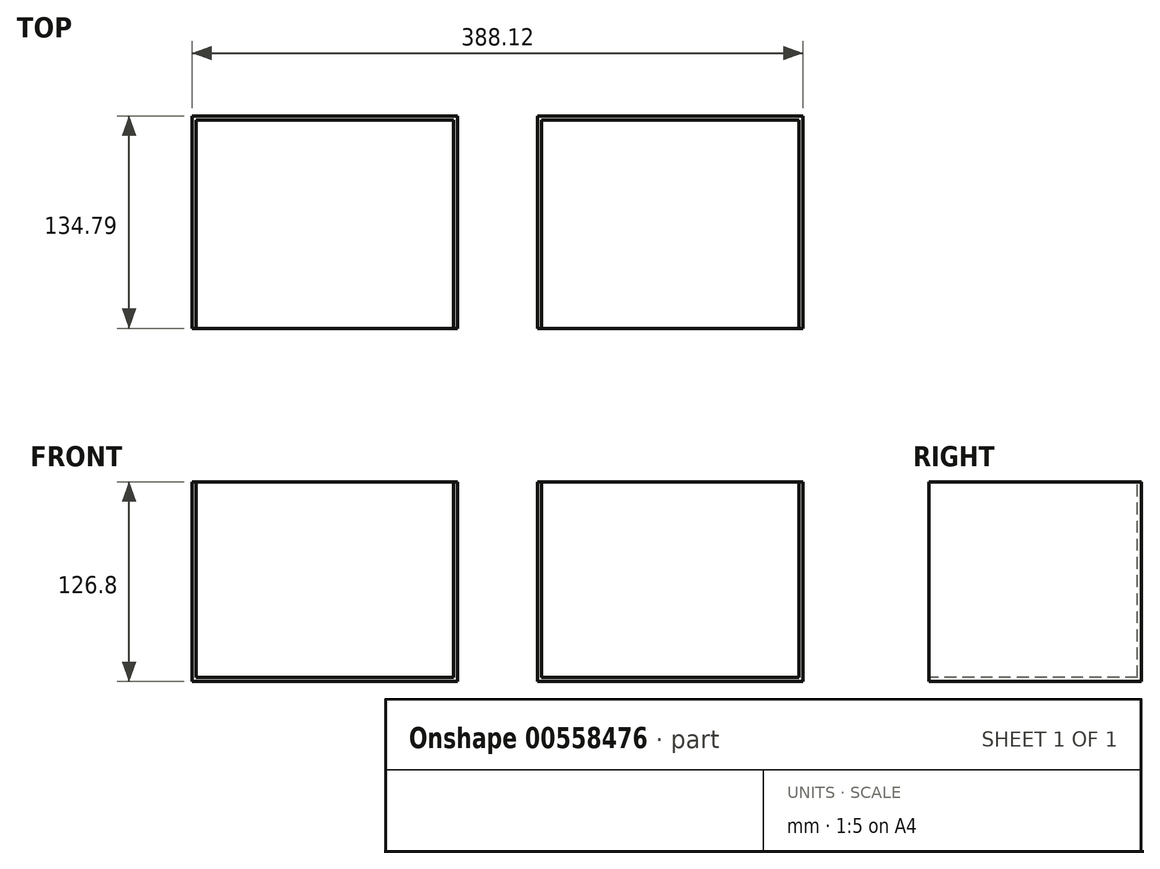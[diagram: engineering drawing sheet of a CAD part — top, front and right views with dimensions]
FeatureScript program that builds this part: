
annotation { "Feature Type Name" : "Feature", "Feature Type Description" : "" }
export const myFeature = defineFeature(function(context is Context, id is Id, definition is map)
    precondition{}
    {
        {
            var Q0;
            Q0=qCreatedBy(makeId("Front.planeOp"),FACE);
            var sketch = newSketch(context, id + "F0", { "sketchPlane" : qUnion([Q0])});
            skLineSegment(sketch, "E0.bottom", {"start": v(60.56, 0) * mm, "end": v(-108.1, 0) * mm});
            skLineSegment(sketch, "E0.top", {"start": v(60.56, 126.8) * mm, "end": v(-108.1, 126.8) * mm});
            skLineSegment(sketch, "E0.left", {"start": v(60.56, 0) * mm, "end": v(60.56, 126.8) * mm});
            skLineSegment(sketch, "E0.right", {"start": v(-108.1, 0) * mm, "end": v(-108.1, 126.8) * mm});
            skSolve(sketch);
        }
        {
            var Q0;
            Q0 = qSketchRegion(id + "F0", true);
            extrude(context, id + "F1", {"entities" : qUnion([Q0]), "oppositeDirection" : true, "depth" : 134.8 * mm, "offsetDistance" : 25.4 * mm});
        }
        {
            var Q0;
            Q0=makeQuery(id+"F1.opExtrude","CAP_FACE",FACE,{"disambiguationData":[OSD([sQuery(id+"F0.wireOp",EDGE,"E0.bottom"),sQuery(id+"F0.wireOp",EDGE,"E0.top"),sQuery(id+"F0.wireOp",EDGE,"E0.left"),sQuery(id+"F0.wireOp",EDGE,"E0.right")])],"isStart":true});
            var Q1;
            Q1=makeQuery(id+"F1.opExtrude","SWEPT_FACE",FACE,{"disambiguationData":[OSD([sQuery(id+"F0.wireOp",EDGE,"E0.top")])]});
            shell(context, id + "F2", {"entities" : qUnion([Q0, Q1]), "thickness" : 2.54 * mm});
        }
        {
            var Q0;
            Q0=makeQuery(id+"F1.opExtrude","SWEPT_FACE",FACE,{"disambiguationData":[OSD([sQuery(id+"F0.wireOp",EDGE,"E0.right")])]});
            cPlane(context, id + "F3", {"entities" : qUnion([Q0]), "cplaneType" : CPlaneType.OFFSET, "offset" : 25.4 * mm, "width" : 152.4 * mm, "height" : 152.4 * mm});
        }
        {
            var Q0;
            Q0=makeQuery(id+"F1.opExtrude","SWEPT_BODY",BODY,{"disambiguationData":[OSD([sQuery(id+"F0.wireOp",EDGE,"E0.bottom"),sQuery(id+"F0.wireOp",EDGE,"E0.top"),sQuery(id+"F0.wireOp",EDGE,"E0.left"),sQuery(id+"F0.wireOp",EDGE,"E0.right")])]});
            var Q1;
            Q1=qCreatedBy(id+"F3.planeOp",FACE);
            mirror(context, id + "F4", {"entities" : qUnion([Q0]), "mirrorPlane" : qUnion([Q1])});
        }
    });
